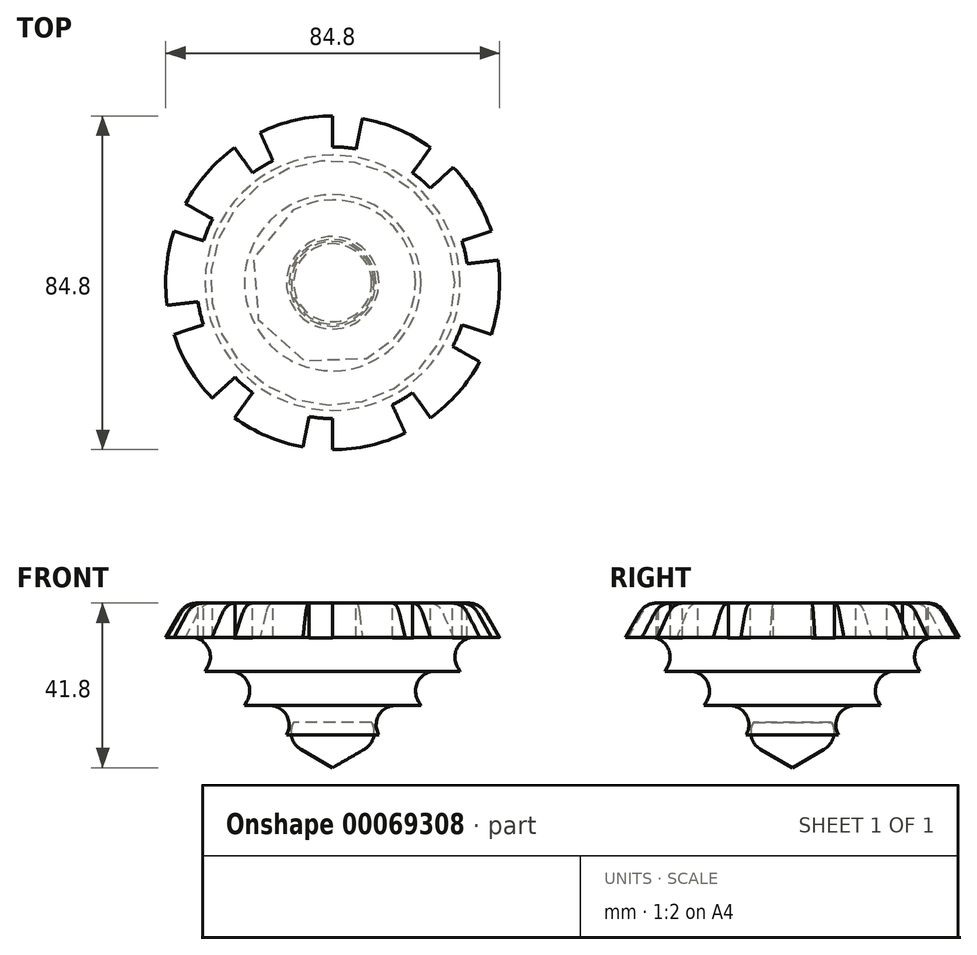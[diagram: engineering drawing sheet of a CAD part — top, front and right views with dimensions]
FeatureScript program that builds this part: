
annotation { "Feature Type Name" : "Feature", "Feature Type Description" : "" }
export const myFeature = defineFeature(function(context is Context, id is Id, definition is map)
    precondition{}
    {
        {
            var Q0;
            Q0=qCreatedBy(makeId("Front.planeOp"),FACE);
            var sketch = newSketch(context, id + "F0", { "sketchPlane" : qUnion([Q0])});
            skLineSegment(sketch, "E0", {"start": v(11.73, -53.09) * mm, "end": v(9.9, -49.92) * mm});
            skLineSegment(sketch, "E1", {"start": v(16.06, -45.59) * mm, "end": v(22.4, -45.59) * mm});
            skLineSegment(sketch, "E2", {"start": v(22.4, -45.59) * mm, "end": v(21.73, -44.43) * mm});
            skLineSegment(sketch, "E3", {"start": v(26.06, -36.93) * mm, "end": v(32.4, -36.93) * mm});
            skLineSegment(sketch, "E4", {"start": v(32.4, -36.93) * mm, "end": v(31.73, -35.77) * mm});
            skLineSegment(sketch, "E5", {"start": v(36.06, -28.27) * mm, "end": v(42.4, -28.27) * mm});
            skLineSegment(sketch, "E6", {"start": v(42.4, -28.27) * mm, "end": v(38.85, -22.1) * mm});
            skLineSegment(sketch, "E7", {"start": v(8.07, -56.75) * mm, "end": v(0, -61.41) * mm});
            skLineSegment(sketch, "E8", {"start": v(34.52, -19.6) * mm, "end": v(0, -19.6) * mm});
            skLineSegment(sketch, "E9", {"start": v(0, -19.6) * mm, "end": v(0, -61.41) * mm});
            skPoint(sketch, "E10.visualSharp", {"position": v(12.4, -54.25) * mm});
            skArc(sketch, "E10.filletArc", {"start": v(8.07, -56.75) * mm, "mid": v(10.4, -53.71) * mm, "end": v(9.9, -49.92) * mm});
            skPoint(sketch, "E11.visualSharp", {"position": v(7.4, -45.59) * mm});
            skArc(sketch, "E11.filletArc", {"start": v(16.06, -45.59) * mm, "mid": v(11.73, -48.09) * mm, "end": v(11.73, -53.09) * mm});
            skPoint(sketch, "E12.visualSharp", {"position": v(17.4, -36.93) * mm});
            skArc(sketch, "E12.filletArc", {"start": v(26.06, -36.93) * mm, "mid": v(21.73, -39.43) * mm, "end": v(21.73, -44.43) * mm});
            skPoint(sketch, "E13.visualSharp", {"position": v(27.4, -28.27) * mm});
            skArc(sketch, "E13.filletArc", {"start": v(36.06, -28.27) * mm, "mid": v(31.73, -30.77) * mm, "end": v(31.73, -35.77) * mm});
            skPoint(sketch, "E14.visualSharp", {"position": v(37.4, -19.6) * mm});
            skArc(sketch, "E14.filletArc", {"start": v(38.85, -22.1) * mm, "mid": v(37.02, -20.28) * mm, "end": v(34.52, -19.6) * mm});
            skSolve(sketch);
        }
        {
            var Q0;
            Q0=makeQuery(id+"F0.imprint","IMPRINT",FACE,{"disambiguationData":[TD([[makeQuery(id+"F0.imprint","IMPRINT",EDGE,{"derivedFrom":sQuery(id+"F0.wireOp",EDGE,"E0")}),-1.0]])]});
            var Q1;
            Q1=sQuery(id+"F0.wireOp",EDGE,"E9");
            revolve(context, id + "F1", {"entities" : qUnion([Q0]), "axis" : qUnion([Q1]), "revolveType" : RevolveType.FULL});
        }
        {
            var Q0;
            Q0=makeQuery(id+"F1.opRevolve","SWEPT_FACE",FACE,{"disambiguationData":[OSD([sQuery(id+"F0.wireOp",EDGE,"E8")])]});
            var sketch = newSketch(context, id + "F2", { "sketchPlane" : qUnion([Q0])});
            skSolve(sketch);
        }
        {
            var Q0;
            Q0=makeQuery(id+"F2.imprint","IMPRINT",FACE,{"disambiguationData":[TD([[makeQuery(id+"F2.imprint","IMPRINT",EDGE,{"derivedFrom":makeQuery(id+"F1.opRevolve","SWEPT_EDGE",EDGE,{"disambiguationData":[OSD([sQuery(id+"F0.wireOp",EDGE,"E8"),sQuery(id+"F0.wireOp",EDGE,"E14.filletArc")])]})}),1.0]])]});
            var sketch = newSketch(context, id + "F3", { "sketchPlane" : qUnion([Q0])});
            skCircle(sketch, "E15", {"center": v(0, 0) * mm, "radius": 4.66 * mm});
            skLineSegment(sketch, "E16", {"start": v(0, -4.66) * mm, "end": v(0, -44.01) * mm});
            skLineSegment(sketch, "E17", {"start": v(0, -44.01) * mm, "end": v(-8, -44.01) * mm});
            skLineSegment(sketch, "E18", {"start": v(-8, -44.01) * mm, "end": v(0, -4.66) * mm});
            skLineSegment(sketch, "E19.1.0", {"start": v(25.87, -35.6) * mm, "end": v(19.4, -40.3) * mm});
            skLineSegment(sketch, "E19.1.1", {"start": v(2.74, -3.77) * mm, "end": v(25.87, -35.6) * mm});
            skLineSegment(sketch, "E19.1.2", {"start": v(19.4, -40.3) * mm, "end": v(2.74, -3.77) * mm});
            skLineSegment(sketch, "E19.2.0", {"start": v(41.86, -13.6) * mm, "end": v(39.38, -21.2) * mm});
            skLineSegment(sketch, "E19.2.1", {"start": v(4.43, -1.44) * mm, "end": v(41.86, -13.6) * mm});
            skLineSegment(sketch, "E19.2.2", {"start": v(39.38, -21.2) * mm, "end": v(4.43, -1.44) * mm});
            skLineSegment(sketch, "E19.3.0", {"start": v(41.86, 13.6) * mm, "end": v(44.33, 6) * mm});
            skLineSegment(sketch, "E19.3.1", {"start": v(4.43, 1.44) * mm, "end": v(41.86, 13.6) * mm});
            skLineSegment(sketch, "E19.3.2", {"start": v(44.33, 6) * mm, "end": v(4.43, 1.44) * mm});
            skLineSegment(sketch, "E19.4.0", {"start": v(25.87, 35.6) * mm, "end": v(32.34, 30.9) * mm});
            skLineSegment(sketch, "E19.4.1", {"start": v(2.74, 3.77) * mm, "end": v(25.87, 35.6) * mm});
            skLineSegment(sketch, "E19.4.2", {"start": v(32.34, 30.9) * mm, "end": v(2.74, 3.77) * mm});
            skLineSegment(sketch, "E19.5.0", {"start": v(0, 44.01) * mm, "end": v(8, 44.01) * mm});
            skLineSegment(sketch, "E19.5.1", {"start": v(0, 4.66) * mm, "end": v(0, 44.01) * mm});
            skLineSegment(sketch, "E19.5.2", {"start": v(8, 44.01) * mm, "end": v(0, 4.66) * mm});
            skLineSegment(sketch, "E19.6.0", {"start": v(-25.87, 35.6) * mm, "end": v(-19.4, 40.3) * mm});
            skLineSegment(sketch, "E19.6.1", {"start": v(-2.74, 3.77) * mm, "end": v(-25.87, 35.6) * mm});
            skLineSegment(sketch, "E19.6.2", {"start": v(-19.4, 40.3) * mm, "end": v(-2.74, 3.77) * mm});
            skLineSegment(sketch, "E19.7.0", {"start": v(-41.86, 13.6) * mm, "end": v(-39.38, 21.2) * mm});
            skLineSegment(sketch, "E19.7.1", {"start": v(-4.43, 1.44) * mm, "end": v(-41.86, 13.6) * mm});
            skLineSegment(sketch, "E19.7.2", {"start": v(-39.38, 21.2) * mm, "end": v(-4.43, 1.44) * mm});
            skLineSegment(sketch, "E19.8.0", {"start": v(-41.86, -13.6) * mm, "end": v(-44.33, -6) * mm});
            skLineSegment(sketch, "E19.8.1", {"start": v(-4.43, -1.44) * mm, "end": v(-41.86, -13.6) * mm});
            skLineSegment(sketch, "E19.8.2", {"start": v(-44.33, -6) * mm, "end": v(-4.43, -1.44) * mm});
            skLineSegment(sketch, "E19.9.0", {"start": v(-25.87, -35.6) * mm, "end": v(-32.34, -30.9) * mm});
            skLineSegment(sketch, "E19.9.1", {"start": v(-2.74, -3.77) * mm, "end": v(-25.87, -35.6) * mm});
            skLineSegment(sketch, "E19.9.2", {"start": v(-32.34, -30.9) * mm, "end": v(-2.74, -3.77) * mm});
            skSolve(sketch);
        }
        {
            var Q0;
            {var subQ0=sQuery(id+"F3.wireOp",EDGE,"E19.6.0");Q0=makeQuery(id+"F3.imprint","IMPRINT",FACE,{"disambiguationData":[TD([[makeQuery(id+"F3.imprint","IMPRINT",EDGE,{"derivedFrom":subQ0}),-1.0]])]});}
            var Q1;
            {var subQ0=sQuery(id+"F3.wireOp",EDGE,"E19.7.0");Q1=makeQuery(id+"F3.imprint","IMPRINT",FACE,{"disambiguationData":[TD([[makeQuery(id+"F3.imprint","IMPRINT",EDGE,{"derivedFrom":subQ0}),-1.0]])]});}
            var Q2;
            {var subQ0=sQuery(id+"F3.wireOp",EDGE,"E19.8.0");Q2=makeQuery(id+"F3.imprint","IMPRINT",FACE,{"disambiguationData":[TD([[makeQuery(id+"F3.imprint","IMPRINT",EDGE,{"derivedFrom":subQ0}),-1.0]])]});}
            var Q3;
            {var subQ0=sQuery(id+"F3.wireOp",EDGE,"E19.9.0");Q3=makeQuery(id+"F3.imprint","IMPRINT",FACE,{"disambiguationData":[TD([[makeQuery(id+"F3.imprint","IMPRINT",EDGE,{"derivedFrom":subQ0}),-1.0]])]});}
            var Q4;
            {var subQ0=sQuery(id+"F3.wireOp",EDGE,"E17");Q4=makeQuery(id+"F3.imprint","IMPRINT",FACE,{"disambiguationData":[TD([[makeQuery(id+"F3.imprint","IMPRINT",EDGE,{"derivedFrom":subQ0}),-1.0]])]});}
            var Q5;
            {var subQ0=sQuery(id+"F3.wireOp",EDGE,"E19.1.0");Q5=makeQuery(id+"F3.imprint","IMPRINT",FACE,{"disambiguationData":[TD([[makeQuery(id+"F3.imprint","IMPRINT",EDGE,{"derivedFrom":subQ0}),-1.0]])]});}
            var Q6;
            {var subQ0=sQuery(id+"F3.wireOp",EDGE,"E19.2.0");Q6=makeQuery(id+"F3.imprint","IMPRINT",FACE,{"disambiguationData":[TD([[makeQuery(id+"F3.imprint","IMPRINT",EDGE,{"derivedFrom":subQ0}),-1.0]])]});}
            var Q7;
            {var subQ0=sQuery(id+"F3.wireOp",EDGE,"E19.3.0");Q7=makeQuery(id+"F3.imprint","IMPRINT",FACE,{"disambiguationData":[TD([[makeQuery(id+"F3.imprint","IMPRINT",EDGE,{"derivedFrom":subQ0}),-1.0]])]});}
            var Q8;
            {var subQ0=sQuery(id+"F3.wireOp",EDGE,"E19.4.0");Q8=makeQuery(id+"F3.imprint","IMPRINT",FACE,{"disambiguationData":[TD([[makeQuery(id+"F3.imprint","IMPRINT",EDGE,{"derivedFrom":subQ0}),-1.0]])]});}
            var Q9;
            {var subQ0=sQuery(id+"F3.wireOp",EDGE,"E19.5.0");Q9=makeQuery(id+"F3.imprint","IMPRINT",FACE,{"disambiguationData":[TD([[makeQuery(id+"F3.imprint","IMPRINT",EDGE,{"derivedFrom":subQ0}),-1.0]])]});}
            extrude(context, id + "F4", {"entities" : qUnion([Q0, Q1, Q2, Q3, Q4, Q5, Q6, Q7, Q8, Q9]), "operationType" : NewBodyOperationType.REMOVE, "oppositeDirection" : true, "depth" : 25 * mm});
        }
    });
